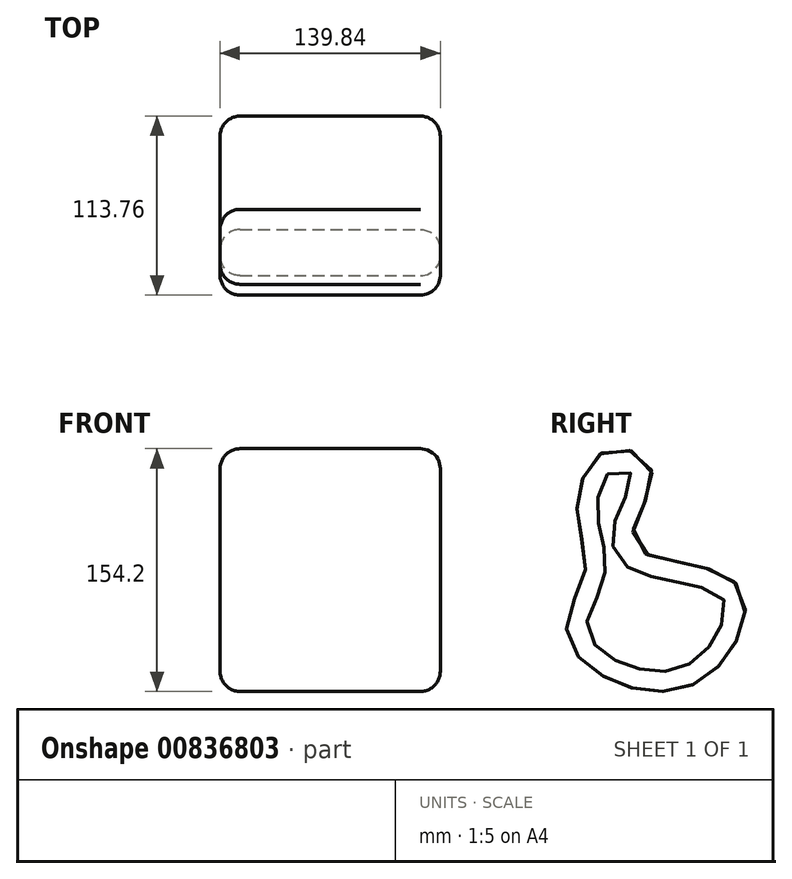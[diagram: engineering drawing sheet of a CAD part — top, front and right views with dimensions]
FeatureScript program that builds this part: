
annotation { "Feature Type Name" : "Feature", "Feature Type Description" : "" }
export const myFeature = defineFeature(function(context is Context, id is Id, definition is map)
    precondition{}
    {
        {
            var Q0;
            Q0=qCreatedBy(makeId("Right.planeOp"),FACE);
            var sketch = newSketch(context, id + "F0", { "sketchPlane" : qUnion([Q0])});
            skFitSpline(sketch, "E0", {"points": [v(-54.37, 37.22) * mm, v(-66.45, 0) * mm, v(-39.36, -32.4) * mm, v(21.42, -31.68) * mm, v(45.58, 22.54) * mm, v(0, 43.06) * mm, v(-24.71, 56.6) * mm, v(-12.26, 100.2) * mm, v(-41.19, 112.66) * mm, v(-59.5, 73.46) * mm, v(-54.37, 37.22) * mm]});
            skSolve(sketch);
        }
        {
            var Q0;
            Q0=makeQuery(id+"F0.imprint","IMPRINT",FACE,{"disambiguationData":[TD([[makeQuery(id+"F0.imprint","IMPRINT",EDGE,{"derivedFrom":sQuery(id+"F0.wireOp",EDGE,"E0")}),1.0]])]});
            extrude(context, id + "F1", {"entities" : qUnion([Q0]), "endBound" : BoundingType.SYMMETRIC, "depth" : 139.84 * mm, "offsetDistance" : 25.4 * mm});
        }
        {
            var Q0;
            Q0=makeQuery(id+"F1.opExtrude","CAP_EDGE",EDGE,{"disambiguationData":[OSD([sQuery(id+"F0.wireOp",EDGE,"E0")])],"isStart":false});
            var Q1;
            Q1=makeQuery(id+"F1.opExtrude","CAP_EDGE",EDGE,{"disambiguationData":[OSD([sQuery(id+"F0.wireOp",EDGE,"E0")])],"isStart":true});
            fillet(context, id + "F2", {"entities" : qUnion([Q0, Q1]), "radius" : 12.7 * mm, "tangentPropagation" : true, "allowEdgeOverflow" : false});
        }
    });
